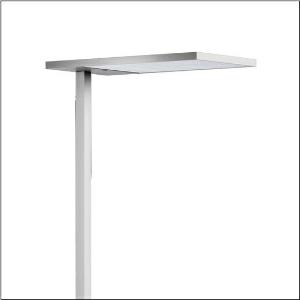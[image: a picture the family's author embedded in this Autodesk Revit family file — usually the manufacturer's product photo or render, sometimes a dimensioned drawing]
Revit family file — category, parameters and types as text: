
# Revit family: silica_21_floor_r_51mx53sg4ds
name_source: partatom
category: Lighting Fixtures
units: mm (PartAtom-declared; Revit-internal decimal feet)

## family parameters
Cut with Voids When Loaded = No
Host = Face
Light Source = No
Part Type = Normal
Room Calculation Point = No
Round Connector Dimension = Use Diameter
Shared = No

## types (1)
- Silica 21 Floor R (1 x LED, 15000 lm, 106.4 W, 4000K)
    Apparent Load = 106 VA
    CIE Flux Codes = 54 86 97 13 100
    Color Rendering = 80
    Color Temperature = 4000K
    Default Elevation = 1800 mm
    Description = Silica® 21 Floor R, floorstanding luminaire, of PMMA, primary optical cover: prismatic diffuser, of PMMA, CAT 2 (L<= 3000cd/m²), light emission: indirect/direct distribution, primary light characteristic: symmetric, primary optical cover: cover panel, of PMMA, installation type: not mounted, LED, rated luminous flux: 15.000lm, luminous efficacy: 141lm/W, light colour: 840, colour temperature: 4000K, control gear: DALI 2, daylight-dependent control, mains connection: 230V, AC, 50/60Hz, connection cable included, cable length: 2,5m, rated input power: 106.4W, luminaire head, of aluminium, powder-coated, metallic grey (RAL 9006), length: 671mm, width: 371mm, height: 2010mm, supporting column, angular, of aluminium, powder-coated, metallic grey (RAL 9006), baseplate, of steel, powder-coated, metallic grey (RAL 9006), sensor module PR3-S, local control - self-sufficient standalone sensors, equipment: master, dimmable, protection rating (complete): IP20, insulation class (complete): insulation class I (protective earthing), certification: CE, permissible operating ambient temperature: 0..+35°C, standard: EN 50419, packaging unit: 1 piece
    Height = 18 mm
    Lamp = 1 x LED
    Lamp Light Flux = 15000 lm
    Lamp Power = 106.4 W
    Lamp count = 1
    Length = 650 mm
    Luminous efficacy = 141 lm/W
    Manufacturer = Siteco
    ModVariant = No
    Model = 51MX53SG4DS
    Mounting Place = Floor
    Mounting Type = Freestanding
    Number of Poles = 1
    OnlyDefault = Yes
    Power Factor = 1
    Product Name = Silica 21 Floor R
    Product group = floorstanding luminaire
    ProductGroupID = 1302
    Protection Class = Protection class I
    Protection Degree = IP 20
    RLX_Detail_Level = 1
    RLX_Emergency_Light_Flux = 0 lm
    RLX_Emergency_Type = 0
    RLX_Emergency_Type_DB = No
    RlxData = <blob elided: 20441 chars, md5=9a1f046d>
    Socket = socket
    Standby Power = 0 W
    System Light Flux = 15000 lm
    System Power = 106 W
    Type Comments = Product without accessories
    Type Image = l_1006716.jpg
    URL = http://relux.com
    VarID = ---
    Voltage = 0 V
    Weight = 0.00 kg
    Width = 350 mm

## geometry (parser evidence)
native form markers: Blend x4, Sweep x15
no freeform markers — native parametric forms only
